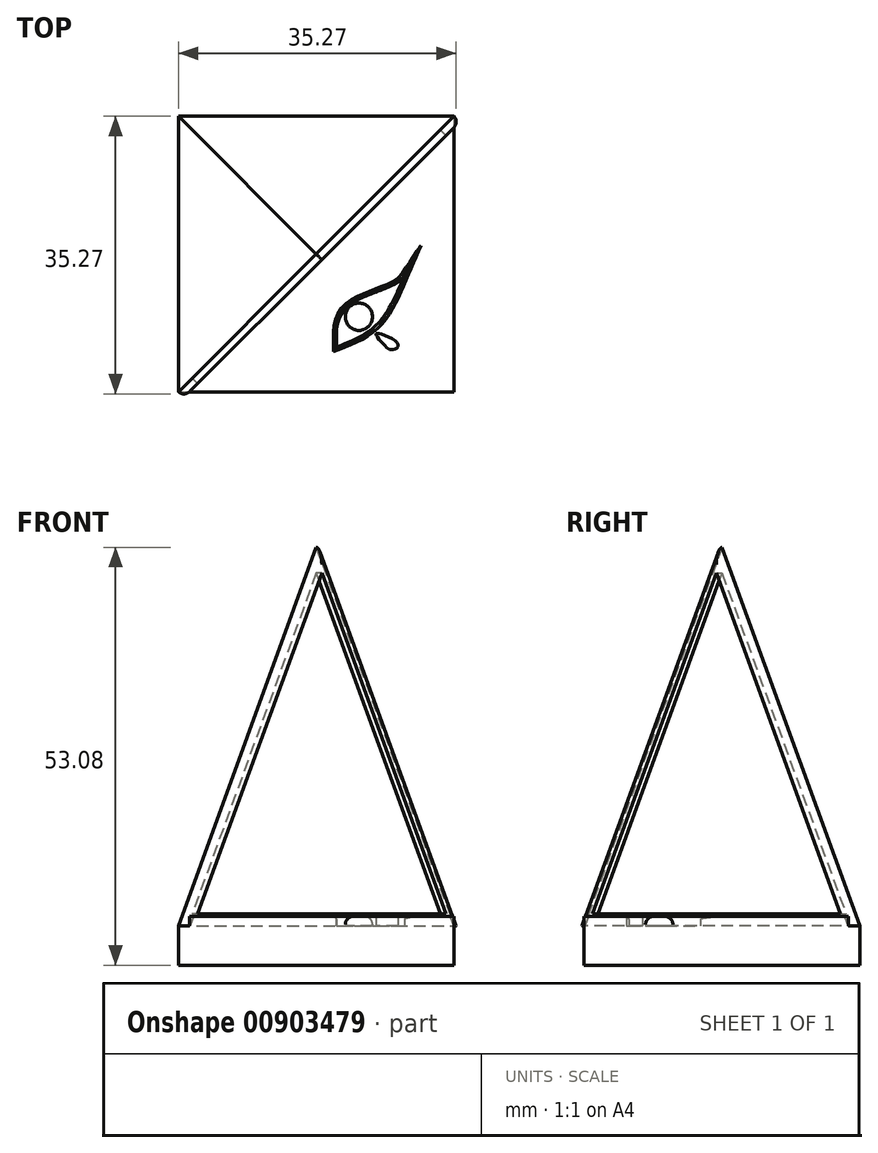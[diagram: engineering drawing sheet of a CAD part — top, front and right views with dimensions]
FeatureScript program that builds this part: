
annotation { "Feature Type Name" : "Feature", "Feature Type Description" : "" }
export const myFeature = defineFeature(function(context is Context, id is Id, definition is map)
    precondition{}
    {
        {
            var Q0;
            Q0=qCreatedBy(makeId("Top.planeOp"),FACE);
            var sketch = newSketch(context, id + "F0", { "sketchPlane" : qUnion([Q0])});
            skLineSegment(sketch, "E0.bottom", {"start": v(-17.5, 17.5) * mm, "end": v(17.5, 17.5) * mm});
            skLineSegment(sketch, "E0.top", {"start": v(-17.5, -17.5) * mm, "end": v(17.5, -17.5) * mm});
            skLineSegment(sketch, "E0.left", {"start": v(-17.5, 17.5) * mm, "end": v(-17.5, -17.5) * mm});
            skLineSegment(sketch, "E0.right", {"start": v(17.5, 17.5) * mm, "end": v(17.5, -17.5) * mm});
            skSolve(sketch);
        }
        {
            var Q0;
            Q0=makeQuery(id+"F0.imprint","IMPRINT",FACE,{"disambiguationData":[TD([[makeQuery(id+"F0.imprint","IMPRINT",EDGE,{"derivedFrom":sQuery(id+"F0.wireOp",EDGE,"E0.bottom")}),-1.0]])]});
            extrude(context, id + "F1", {"entities" : qUnion([Q0]), "depth" : 5 * mm, "offsetDistance" : 25 * mm});
        }
        {
            var Q0;
            Q0=makeQuery(id+"F1.opExtrude","CAP_FACE",FACE,{"disambiguationData":[OSD([sQuery(id+"F0.wireOp",EDGE,"E0.bottom"),sQuery(id+"F0.wireOp",EDGE,"E0.top"),sQuery(id+"F0.wireOp",EDGE,"E0.left"),sQuery(id+"F0.wireOp",EDGE,"E0.right")])],"isStart":false});
            var sketch = newSketch(context, id + "F2", { "sketchPlane" : qUnion([Q0])});
            skLineSegment(sketch, "E1", {"start": v(-17.5, -17.5) * mm, "end": v(17.5, 17.5) * mm});
            skLineSegment(sketch, "E2", {"start": v(17.5, 17.5) * mm, "end": v(17.5, -17.5) * mm});
            skLineSegment(sketch, "E3", {"start": v(17.5, -17.5) * mm, "end": v(-17.5, -17.5) * mm});
            skSolve(sketch);
        }
        {
            var Q0;
            Q0=makeQuery(id+"F1.opExtrude","CAP_FACE",FACE,{"disambiguationData":[OSD([sQuery(id+"F0.wireOp",EDGE,"E0.bottom"),sQuery(id+"F0.wireOp",EDGE,"E0.top"),sQuery(id+"F0.wireOp",EDGE,"E0.left"),sQuery(id+"F0.wireOp",EDGE,"E0.right")])],"isStart":false});
            extrude(context, id + "F3", {"entities" : qUnion([Q0]), "operationType" : NewBodyOperationType.ADD, "depth" : 49.7 * mm, "offsetDistance" : 25 * mm, "hasDraft" : true, "draftAngle" : 20 * degree, "draftPullDirection" : true});
        }
        {
            var Q0;
            Q0 = qSketchRegion(id + "F2", true);
            extrude(context, id + "F4", {"entities" : qUnion([Q0]), "operationType" : NewBodyOperationType.REMOVE, "depth" : 53.3 * mm, "offsetDistance" : 25 * mm});
        }
        {
            var Q0;
            Q0=makeQuery(id+"F4.boolean.opBoolean","COPY",FACE,{"derivedFrom":makeQuery(id+"F4.opExtrude","SWEPT_FACE",FACE,{"disambiguationData":[OSD([sQuery(id+"F2.wireOp",EDGE,"E1")])]})});
            var sketch = newSketch(context, id + "F5", { "sketchPlane" : qUnion([Q0])});
            skLineSegment(sketch, "E4.0", {"start": v(0, 49.8) * mm, "end": v(-22.29, 6.5) * mm});
            skLineSegment(sketch, "E4.1", {"start": v(0, 49.8) * mm, "end": v(22.29, 6.5) * mm});
            skLineSegment(sketch, "E4.2", {"start": v(-22.29, 6.5) * mm, "end": v(22.29, 6.5) * mm});
            skSolve(sketch);
        }
        {
            var Q0;
            Q0=makeQuery(id+"F5.imprint","IMPRINT",FACE,{"disambiguationData":[TD([[makeQuery(id+"F5.imprint","IMPRINT",EDGE,{"derivedFrom":sQuery(id+"F5.wireOp",EDGE,"E4.0")}),-1.0]])]});
            extrude(context, id + "F6", {"entities" : qUnion([Q0]), "operationType" : NewBodyOperationType.ADD, "depth" : 1 * mm, "offsetDistance" : 25 * mm});
        }
        {
            var Q0;
            Q0=makeQuery(id+"F6.opExtrude","CAP_EDGE",EDGE,{"disambiguationData":[OSD([sQuery(id+"F0.wireOp",EDGE,"E0.top"),sQuery(id+"F0.wireOp",EDGE,"E0.left")])],"isStart":false});
            var Q1;
            Q1=makeQuery(id+"F6.opExtrude","CAP_EDGE",EDGE,{"disambiguationData":[OSD([sQuery(id+"F0.wireOp",EDGE,"E0.bottom"),sQuery(id+"F0.wireOp",EDGE,"E0.right")])],"isStart":false});
            fillet(context, id + "F7", {"entities" : qUnion([Q0, Q1]), "radius" : 1 * mm, "tangentPropagation" : true, "allowEdgeOverflow" : false});
        }
        {
            var Q0;
            Q0=makeQuery(id+"F4.boolean.opBoolean","COPY",FACE,{"derivedFrom":makeQuery(id+"F4.opExtrude","CAP_FACE",FACE,{"disambiguationData":[OSD([sQuery(id+"F2.wireOp",EDGE,"E1"),sQuery(id+"F2.wireOp",EDGE,"E2"),sQuery(id+"F2.wireOp",EDGE,"E3")])],"isStart":true})});
            var sketch = newSketch(context, id + "F8", { "sketchPlane" : qUnion([Q0])});
            skFitSpline(sketch, "E5", {"points": [v(2.6, -11.8) * mm, v(2.58, -9.66) * mm, v(3.43, -7.24) * mm, v(6.19, -5.38) * mm, v(9.8, -3.92) * mm, v(11.21, -2.74) * mm], "startDerivative": vector(0.57, 11) * mm, "endDerivative": vector(5.78, 8.67) * mm});
            skFitSpline(sketch, "E6", {"points": [v(2.6, -11.8) * mm, v(7.63, -9.05) * mm, v(11.21, -2.74) * mm], "startDerivative": vector(11.57, 4.45) * mm, "endDerivative": vector(5.78, 13.5) * mm});
            skCircle(sketch, "E7", {"center": v(5.42, -7.97) * mm, "radius": 1.73 * mm});
            skFitSpline(sketch, "E8.0", {"points": [v(2.88, -12.55) * mm, v(3.36, -12.37) * mm, v(4.34, -12) * mm, v(5.81, -11.34) * mm, v(6.99, -10.64) * mm, v(7.87, -9.94) * mm, v(8.48, -9.34) * mm, v(9.04, -8.67) * mm, v(9.71, -7.71) * mm, v(10.45, -6.41) * mm, v(11.22, -4.75) * mm, v(11.7, -3.62) * mm, v(11.95, -3.06) * mm]});
            skFitSpline(sketch, "E9.0", {"points": [v(1.68, -11.6) * mm, v(1.7, -11.36) * mm, v(1.72, -10.9) * mm, v(1.77, -10.16) * mm, v(1.87, -9.37) * mm, v(2.04, -8.5) * mm, v(2.3, -7.74) * mm, v(2.6, -7.14) * mm, v(2.89, -6.71) * mm, v(3.23, -6.33) * mm, v(3.73, -5.86) * mm, v(4.45, -5.37) * mm, v(5.42, -4.89) * mm, v(6.45, -4.48) * mm, v(7.5, -4.12) * mm, v(8.3, -3.83) * mm, v(8.84, -3.6) * mm, v(9.32, -3.36) * mm, v(9.72, -3.07) * mm, v(10.07, -2.67) * mm, v(10.3, -2.34) * mm, v(10.42, -2.16) * mm]});
            skFitSpline(sketch, "E10", {"points": [v(3.9, -12.16) * mm, v(1.68, -12.16) * mm, v(1.68, -11.6) * mm], "startDerivative": vector(-2.52, -0.45) * mm, "endDerivative": vector(0.45, 2.06) * mm});
            skFitSpline(sketch, "E11", {"points": [v(9.95, -2.8) * mm, v(11.44, -1.16) * mm, v(11.74, -3.55) * mm], "startDerivative": vector(3.76, 5.43) * mm, "endDerivative": vector(-0.82, -7) * mm});
            skFitSpline(sketch, "E12", {"points": [v(8.47, -9.33) * mm, v(13.65, -9.49) * mm, v(15.1, -7.18) * mm, v(15.85, -7.71) * mm, v(14.11, -9.95) * mm, v(11.02, -10.27) * mm, v(8.4, -9.4) * mm], "startDerivative": vector(28.34, -8.2) * mm, "endDerivative": vector(-17.66, 4.76) * mm});
            skFitSpline(sketch, "E13", {"points": [v(7.65, -10.1) * mm, v(10.39, -11.48) * mm, v(9.68, -12.16) * mm, v(8.58, -11.48) * mm, v(7.65, -10.1) * mm]});
            skSolve(sketch);
        }
        {
            var Q0;
            Q0=makeQuery(id+"F8.imprint","IMPRINT",FACE,{"disambiguationData":[TD([[makeQuery(id+"F8.imprint","IMPRINT",EDGE,{"derivedFrom":sQuery(id+"F8.wireOp",EDGE,"E5")}),1.0]])]});
            var Q1;
            Q1=makeQuery(id+"F8.imprint","IMPRINT",FACE,{"disambiguationData":[TD([[makeQuery(id+"F8.imprint","IMPRINT",EDGE,{"derivedFrom":sQuery(id+"F8.wireOp",EDGE,"E7")}),1.0]])]});
            var Q2;
            {var subQ0=sQuery(id+"F8.wireOp",EDGE,"E13");var subQ1=makeQuery(id+"F8.imprint","IMPRINT",VERTEX,{"derivedFrom":subQ0});Q2=makeQuery(id+"F8.imprint","IMPRINT",FACE,{"disambiguationData":[TD([[makeQuery(id+"F8.imprint","IMPRINT",EDGE,{"disambiguationData":[TD([[subQ1,-1.0]])],"derivedFrom":subQ0}),-1.0]])]});}
            var Q3;
            {var subQ0=sQuery(id+"F8.wireOp",EDGE,"E12");Q3=makeQuery(id+"F8.imprint","IMPRINT",FACE,{"disambiguationData":[TD([[makeQuery(id+"F8.imprint","IMPRINT",EDGE,{"derivedFrom":subQ0}),-1.0]])]});}
            extrude(context, id + "F9", {"entities" : qUnion([Q0, Q1, Q2, Q3]), "operationType" : NewBodyOperationType.ADD, "depth" : 1.2 * mm, "offsetDistance" : 25 * mm});
        }
        {
            var Q0;
            Q0=makeQuery(id+"F9.opExtrude","CAP_EDGE",EDGE,{"disambiguationData":[OSD([sQuery(id+"F8.wireOp",EDGE,"E7")])],"isStart":false});
            fillet(context, id + "F10", {"entities" : qUnion([Q0]), "radius" : 1 * mm, "tangentPropagation" : true, "allowEdgeOverflow" : false});
        }
        {
            var Q0;
            Q0=makeQuery(id+"F9.opExtrude","CAP_EDGE",EDGE,{"disambiguationData":[OSD([sQuery(id+"F8.wireOp",EDGE,"E6")])],"isStart":false});
            var Q1;
            Q1=makeQuery(id+"F9.opExtrude","CAP_EDGE",EDGE,{"disambiguationData":[OSD([sQuery(id+"F8.wireOp",EDGE,"E5")])],"isStart":false});
            fillet(context, id + "F11", {"entities" : qUnion([Q0, Q1]), "radius" : 0.4 * mm, "tangentPropagation" : true, "allowEdgeOverflow" : false});
        }
    });
